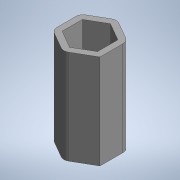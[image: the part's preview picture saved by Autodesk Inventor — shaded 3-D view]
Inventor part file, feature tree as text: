
AUTODESK INVENTOR PART (.ipt)
format: ipt  version: 2022.3 (Build 263350000, 350)  size: 92,672 bytes
history: native  units: mm (DEFAULTED — no unit token found)
features: extrude x1, fillet x1, sketch x1
ambient origin geometry x8: Origin, YZ Plane, XZ Plane, XY Plane, X Axis, Y Axis, Z Axis, Center Point
bodies: Solid1 (feature_tree)
feature tree (3):
  extrude  "Extrusion1"  Depth=9.525mm
  fillet  "Fillet1"  Radius=25.4mm
  sketch  "Sketch1"  dims[d0=12.7mm d2=9.525mm d3=25.4mm d4=0.0mm d5=2.0mm]
